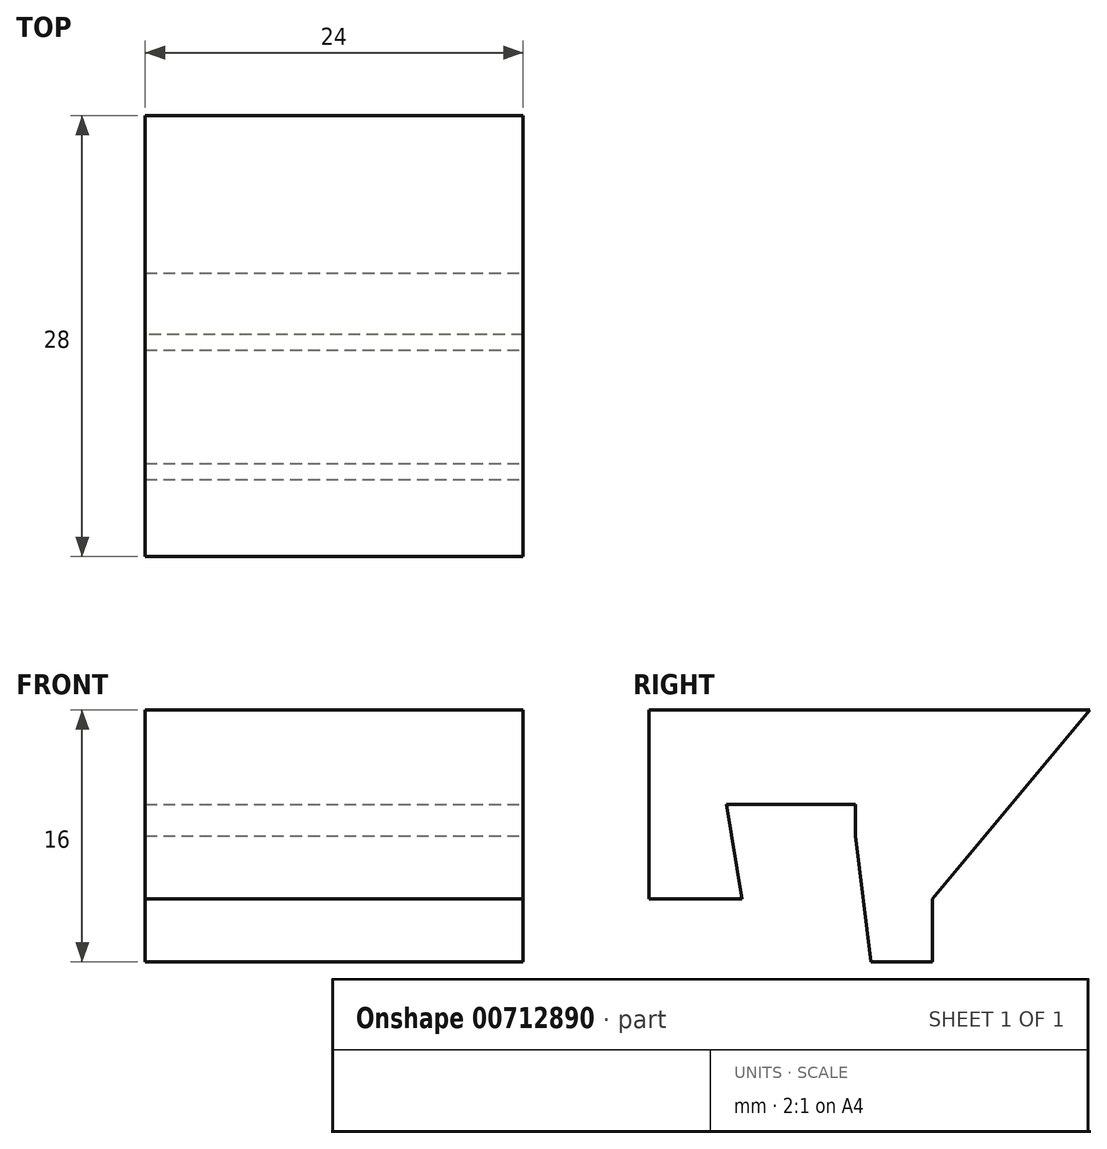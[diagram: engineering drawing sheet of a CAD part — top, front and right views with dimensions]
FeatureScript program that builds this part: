
annotation { "Feature Type Name" : "Feature", "Feature Type Description" : "" }
export const myFeature = defineFeature(function(context is Context, id is Id, definition is map)
    precondition{}
    {
        {
            var Q0;
            Q0=qCreatedBy(makeId("Top.planeOp"),FACE);
            var sketch = newSketch(context, id + "F0", { "sketchPlane" : qUnion([Q0])});
            skLineSegment(sketch, "E0", {"start": v(0, 0) * mm, "end": v(-100, 0) * mm, "construction": true});
            skLineSegment(sketch, "E1.bottom", {"start": v(-100, 0) * mm, "end": v(-76, 0) * mm});
            skLineSegment(sketch, "E1.top", {"start": v(-100, -18) * mm, "end": v(-76, -18) * mm});
            skLineSegment(sketch, "E1.left", {"start": v(-100, 0) * mm, "end": v(-100, -18) * mm});
            skLineSegment(sketch, "E1.right", {"start": v(-76, 0) * mm, "end": v(-76, -18) * mm});
            skLineSegment(sketch, "E2.bottom", {"start": v(-100, -9) * mm, "end": v(-76, -9) * mm});
            skLineSegment(sketch, "E2.top", {"start": v(-100, -4.9) * mm, "end": v(-76, -4.9) * mm});
            skLineSegment(sketch, "E2.left", {"start": v(-100, -9) * mm, "end": v(-100, -4.9) * mm});
            skLineSegment(sketch, "E2.right", {"start": v(-76, -9) * mm, "end": v(-76, -4.9) * mm});
            skLineSegment(sketch, "E3.top", {"start": v(-100, -13.1) * mm, "end": v(-76, -13.1) * mm});
            skLineSegment(sketch, "E3.left", {"start": v(-100, -9) * mm, "end": v(-100, -13.1) * mm});
            skLineSegment(sketch, "E3.right", {"start": v(-76, -9) * mm, "end": v(-76, -13.1) * mm});
            skSolve(sketch);
        }
        {
            var Q0;
            {var subQ0=sQuery(id+"F0.wireOp",EDGE,"E1.bottom");Q0=makeQuery(id+"F0.imprint","IMPRINT",FACE,{"disambiguationData":[TD([[makeQuery(id+"F0.imprint","IMPRINT",EDGE,{"derivedFrom":subQ0}),-1.0]])]});}
            var Q1;
            Q1=makeQuery(id+"F0.imprint","IMPRINT",FACE,{"disambiguationData":[TD([[makeQuery(id+"F0.imprint","IMPRINT",EDGE,{"derivedFrom":sQuery(id+"F0.wireOp",EDGE,"E2.top")}),-1.0]])]});
            var Q2;
            Q2=makeQuery(id+"F0.imprint","IMPRINT",FACE,{"disambiguationData":[TD([[makeQuery(id+"F0.imprint","IMPRINT",EDGE,{"derivedFrom":sQuery(id+"F0.wireOp",EDGE,"E2.bottom")}),-1.0]])]});
            var Q3;
            {var subQ0=sQuery(id+"F0.wireOp",EDGE,"E1.top");Q3=makeQuery(id+"F0.imprint","IMPRINT",FACE,{"disambiguationData":[TD([[makeQuery(id+"F0.imprint","IMPRINT",EDGE,{"derivedFrom":subQ0}),1.0]])]});}
            extrude(context, id + "F1", {"entities" : qUnion([Q0, Q1, Q2, Q3]), "depth" : 12 * mm, "offsetDistance" : 25 * mm});
        }
        {
            var Q0;
            Q0=makeQuery(id+"F0.imprint","IMPRINT",FACE,{"disambiguationData":[TD([[makeQuery(id+"F0.imprint","IMPRINT",EDGE,{"derivedFrom":sQuery(id+"F0.wireOp",EDGE,"E2.top")}),-1.0]])]});
            var Q1;
            Q1=makeQuery(id+"F0.imprint","IMPRINT",FACE,{"disambiguationData":[TD([[makeQuery(id+"F0.imprint","IMPRINT",EDGE,{"derivedFrom":sQuery(id+"F0.wireOp",EDGE,"E2.bottom")}),-1.0]])]});
            var Q2;
            Q2=sQuery(id+"F0.wireOp",EDGE,"E2.top");
            var Q3;
            Q3=sQuery(id+"F0.wireOp",EDGE,"E2.left");
            var Q4;
            Q4=sQuery(id+"F0.wireOp",EDGE,"E3.left");
            var Q5;
            Q5=sQuery(id+"F0.wireOp",EDGE,"E3.top");
            var Q6;
            Q6=sQuery(id+"F0.wireOp",EDGE,"E3.right");
            var Q7;
            Q7=sQuery(id+"F0.wireOp",EDGE,"E2.right");
            extrude(context, id + "F2", {"entities" : qUnion([Q0, Q1]), "operationType" : NewBodyOperationType.REMOVE, "surfaceEntities" : qUnion([Q2, Q3, Q4, Q5, Q6, Q7]), "depth" : 6 * mm, "offsetDistance" : 25 * mm});
        }
        {
            var Q0;
            Q0=makeQuery(id+"F1.opExtrude","SWEPT_FACE",FACE,{"disambiguationData":[OSD([sQuery(id+"F0.wireOp",EDGE,"E1.bottom")])]});
            extrude(context, id + "F3", {"entities" : qUnion([Q0]), "operationType" : NewBodyOperationType.ADD, "depth" : 10 * mm, "offsetDistance" : 25 * mm});
        }
        {
            var Q0;
            {var subQ0=sQuery(id+"F0.wireOp",EDGE,"E1.bottom");Q0=makeQuery(id+"F3.opExtrude","CAP_EDGE",EDGE,{"disambiguationData":[OSD([subQ0]),TDD([makeQuery(id+"F1.opExtrude","CAP_EDGE",EDGE,{"disambiguationData":[OSD([subQ0])],"isStart":true})])],"isStart":false});}
            chamfer(context, id + "F4", {"entities" : qUnion([Q0]), "chamferType" : ChamferType.TWO_OFFSETS, "width1" : 10 * mm, "oppositeDirection" : false, "width2" : 12 * mm, "tangentPropagation" : true});
        }
        {
            var Q0;
            {var subQ0=sQuery(id+"F0.wireOp",EDGE,"E1.right");Q0=makeQuery(id+"F3.boolean.opBoolean","MERGE",FACE,{"derivedFrom":[makeQuery(id+"F1.opExtrude","SWEPT_FACE",FACE,{"disambiguationData":[OSD([subQ0,sQuery(id+"F0.wireOp",EDGE,"E2.right"),sQuery(id+"F0.wireOp",EDGE,"E3.right")])]}),makeQuery(id+"F3.opExtrude","SWEPT_FACE",FACE,{"disambiguationData":[OSD([sQuery(id+"F0.wireOp",EDGE,"E1.bottom"),subQ0])]})]});}
            var sketch = newSketch(context, id + "F5", { "sketchPlane" : qUnion([Q0])});
            skLineSegment(sketch, "E4", {"start": v(-12.1, 0) * mm, "end": v(-13.1, 6) * mm});
            skLineSegment(sketch, "E5", {"start": v(-13.1, 6) * mm, "end": v(-13.1, 0) * mm});
            skLineSegment(sketch, "E6", {"start": v(-13.1, 0) * mm, "end": v(-12.1, 0) * mm});
            skSolve(sketch);
        }
        {
            var Q0;
            Q0=makeQuery(id+"F5.imprint","IMPRINT",FACE,{"disambiguationData":[TD([[makeQuery(id+"F5.imprint","IMPRINT",EDGE,{"derivedFrom":sQuery(id+"F5.wireOp",EDGE,"E4")}),1.0]])]});
            var Q1;
            {var subQ0=sQuery(id+"F0.wireOp",EDGE,"E1.left");Q1=makeQuery(id+"F3.boolean.opBoolean","MERGE",FACE,{"derivedFrom":[makeQuery(id+"F1.opExtrude","SWEPT_FACE",FACE,{"disambiguationData":[OSD([subQ0,sQuery(id+"F0.wireOp",EDGE,"E2.left"),sQuery(id+"F0.wireOp",EDGE,"E3.left")])]}),makeQuery(id+"F3.opExtrude","SWEPT_FACE",FACE,{"disambiguationData":[OSD([sQuery(id+"F0.wireOp",EDGE,"E1.bottom"),subQ0])]})]});}
            extrude(context, id + "F6", {"entities" : qUnion([Q0]), "operationType" : NewBodyOperationType.ADD, "endBound" : BoundingType.UP_TO_SURFACE, "oppositeDirection" : true, "depth" : 25 * mm, "endBoundEntityFace" : qUnion([Q1]), "offsetDistance" : 25 * mm});
        }
        {
            var Q0;
            {var subQ0=sQuery(id+"F0.wireOp",EDGE,"E1.bottom");var subQ1=sQuery(id+"F0.wireOp",EDGE,"E3.right");var subQ2=sQuery(id+"F0.wireOp",EDGE,"E2.right");var subQ3=sQuery(id+"F0.wireOp",EDGE,"E1.right");var subQ4=sQuery(id+"F0.wireOp",EDGE,"E3.left");var subQ5=sQuery(id+"F0.wireOp",EDGE,"E2.left");var subQ6=sQuery(id+"F0.wireOp",EDGE,"E1.left");Q0=makeQuery(id+"F3.boolean.opBoolean","MERGE",FACE,{"derivedFrom":[makeQuery(id+"F2.boolean.opBoolean","SPLIT",FACE,{"disambiguationData":[TD([makeQuery(id+"F1.opExtrude","SWEPT_FACE",FACE,{"disambiguationData":[OSD([subQ0])]})])],"derivedFrom":makeQuery(id+"F1.opExtrude","CAP_FACE",FACE,{"disambiguationData":[OSD([subQ0,sQuery(id+"F0.wireOp",EDGE,"E1.top"),subQ6,subQ3,subQ5,subQ2,subQ4,subQ1])],"isStart":true})}),makeQuery(id+"F3.opExtrude","SWEPT_FACE",FACE,{"disambiguationData":[OSD([subQ0]),TDD([makeQuery(id+"F1.opExtrude","CAP_EDGE",EDGE,{"disambiguationData":[OSD([subQ0])],"isStart":true})])]})]});}
            extrude(context, id + "F7", {"entities" : qUnion([Q0]), "operationType" : NewBodyOperationType.ADD, "depth" : 4 * mm, "offsetDistance" : 25 * mm});
        }
        {
            var Q0;
            Q0=makeQuery(id+"F7.opExtrude","CAP_EDGE",EDGE,{"disambiguationData":[OSD([sQuery(id+"F0.wireOp",EDGE,"E2.top")])],"isStart":false});
            chamfer(context, id + "F8", {"entities" : qUnion([Q0]), "chamferType" : ChamferType.TWO_OFFSETS, "width1" : 8 * mm, "oppositeDirection" : false, "width2" : 1 * mm, "tangentPropagation" : true});
        }
    });
